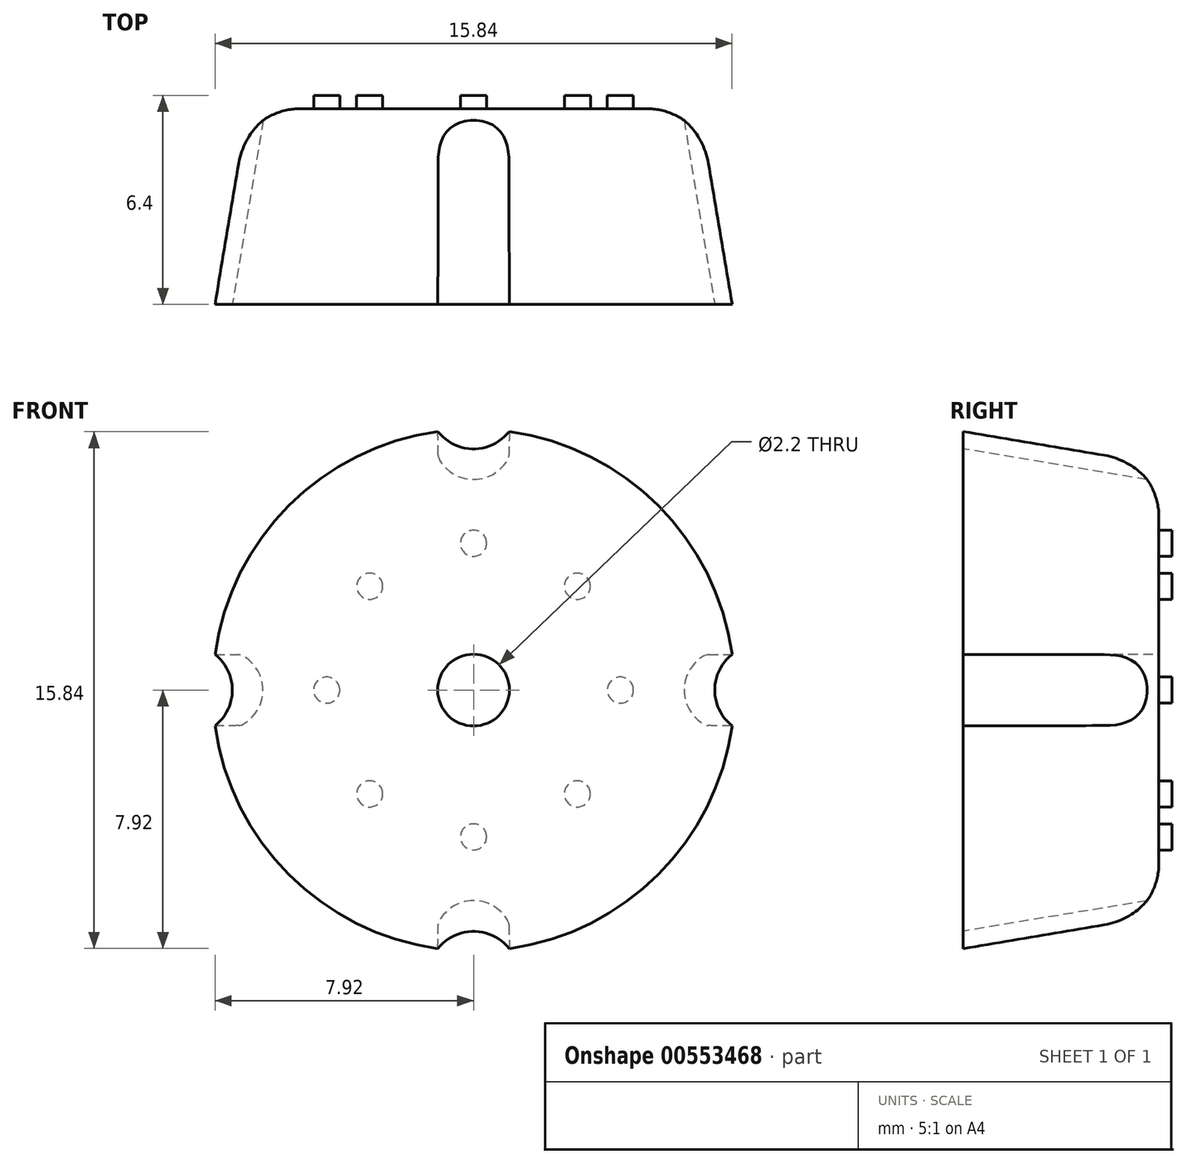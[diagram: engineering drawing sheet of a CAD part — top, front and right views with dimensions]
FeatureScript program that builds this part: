
annotation { "Feature Type Name" : "Feature", "Feature Type Description" : "" }
export const myFeature = defineFeature(function(context is Context, id is Id, definition is map)
    precondition{}
    {
        {
            var Q0;
            Q0=qCreatedBy(makeId("Top.planeOp"),FACE);
            var sketch = newSketch(context, id + "F0", { "sketchPlane" : qUnion([Q0])});
            skLineSegment(sketch, "E0", {"start": v(0, 0) * mm, "end": v(0, 26.8) * mm, "construction": true});
            skLineSegment(sketch, "E1", {"start": v(0, 0) * mm, "end": v(-8, 0) * mm});
            skLineSegment(sketch, "E2", {"start": v(-8, 0) * mm, "end": v(-7.28, 4.33) * mm});
            skLineSegment(sketch, "E3", {"start": v(-5.3, 6) * mm, "end": v(0, 6) * mm});
            skLineSegment(sketch, "E4", {"start": v(0, 6) * mm, "end": v(0, 0) * mm});
            skPoint(sketch, "E5.visualSharp", {"position": v(-7, 6) * mm});
            skArc(sketch, "E5.filletArc", {"start": v(-5.3, 6) * mm, "mid": v(-6.6, 5.53) * mm, "end": v(-7.28, 4.33) * mm});
            skSolve(sketch);
        }
        {
            var Q0;
            Q0 = qSketchRegion(id + "F0", true);
            var Q1;
            Q1=sQuery(id+"F0.wireOp",EDGE,"E0");
            revolve(context, id + "F1", {"entities" : qUnion([Q0]), "axis" : qUnion([Q1]), "revolveType" : RevolveType.FULL});
        }
        {
            var Q0;
            Q0=makeQuery(id+"F1.opRevolve","SWEPT_FACE",FACE,{"disambiguationData":[OSD([sQuery(id+"F0.wireOp",EDGE,"E3")])]});
            var sketch = newSketch(context, id + "F2", { "sketchPlane" : qUnion([Q0])});
            skCircle(sketch, "E6", {"center": v(0, 0) * mm, "radius": 4.5 * mm, "construction": true});
            skCircle(sketch, "E7", {"center": v(0, 4.5) * mm, "radius": 0.4 * mm});
            skCircle(sketch, "E8", {"center": v(4.5, 0) * mm, "radius": 0.4 * mm});
            skCircle(sketch, "E9", {"center": v(0, -4.5) * mm, "radius": 0.4 * mm});
            skCircle(sketch, "E10", {"center": v(-4.5, 0) * mm, "radius": 0.4 * mm});
            skLineSegment(sketch, "E11", {"start": v(-6.52, 6.52) * mm, "end": v(7.02, -7.02) * mm, "construction": true});
            skLineSegment(sketch, "E12", {"start": v(-6.76, -6.76) * mm, "end": v(6.87, 6.87) * mm, "construction": true});
            skCircle(sketch, "E13", {"center": v(-3.18, 3.18) * mm, "radius": 0.4 * mm});
            skCircle(sketch, "E14", {"center": v(3.18, 3.18) * mm, "radius": 0.4 * mm});
            skCircle(sketch, "E15", {"center": v(3.18, -3.18) * mm, "radius": 0.4 * mm});
            skCircle(sketch, "E16", {"center": v(-3.18, -3.18) * mm, "radius": 0.4 * mm});
            skSolve(sketch);
        }
        {
            var Q0;
            Q0 = qSketchRegion(id + "F2", true);
            extrude(context, id + "F3", {"entities" : qUnion([Q0]), "operationType" : NewBodyOperationType.ADD, "depth" : 0.4 * mm, "offsetDistance" : 25 * mm});
        }
        {
            var Q0;
            Q0=qCreatedBy(makeId("Right.planeOp"),FACE);
            var sketch = newSketch(context, id + "F4", { "sketchPlane" : qUnion([Q0])});
            skLineSegment(sketch, "E17", {"start": v(-1.6, 9.08) * mm, "end": v(12.64, 6.7) * mm, "construction": true});
            skLineSegment(sketch, "E18", {"start": v(0, 8) * mm, "end": v(4.33, 7.28) * mm, "construction": true});
            skLineSegment(sketch, "E19", {"start": v(4.33, -7.28) * mm, "end": v(0, -8) * mm, "construction": true});
            skLineSegment(sketch, "E20.0", {"start": v(4.33, -7.28) * mm, "end": v(4.33, 7.28) * mm, "construction": true});
            skLineSegment(sketch, "E21", {"start": v(-0.67, 8.92) * mm, "end": v(-0.44, 10.3) * mm});
            skLineSegment(sketch, "E22", {"start": v(-0.44, 10.3) * mm, "end": v(6.8, 9.1) * mm});
            skLineSegment(sketch, "E23", {"start": v(6.8, 9.1) * mm, "end": v(6.58, 7.71) * mm});
            skLineSegment(sketch, "E24", {"start": v(6.58, 7.71) * mm, "end": v(-0.67, 8.92) * mm});
            skSolve(sketch);
        }
        {
            var Q0;
            Q0 = qSketchRegion(id + "F4", true);
            var Q1;
            Q1=sQuery(id+"F4.wireOp",EDGE,"E17");
            revolve(context, id + "F5", {"entities" : qUnion([Q0]), "axis" : qUnion([Q1]), "revolveType" : RevolveType.FULL});
        }
        {
            var Q0;
            Q0=makeQuery(id+"F5.opRevolve","SWEPT_BODY",BODY,{"disambiguationData":[OSD([sQuery(id+"F4.wireOp",EDGE,"E21"),sQuery(id+"F4.wireOp",EDGE,"E22"),sQuery(id+"F4.wireOp",EDGE,"E23"),sQuery(id+"F4.wireOp",EDGE,"E24")])]});
            var Q1;
            Q1=makeQuery(id+"F1.opRevolve","SWEPT_EDGE",EDGE,{"disambiguationData":[OSD([sQuery(id+"F0.wireOp",EDGE,"E1"),sQuery(id+"F0.wireOp",EDGE,"E2")])]});
            circularPattern(context, id + "F6", {"entities" : qUnion([Q0]), "axis" : qUnion([Q1]), "angle" : 360 * degree, "instanceCount" : 4, "equalSpace" : true});
        }
        {
            var Q0;
            Q0=makeQuery(id+"F5.opRevolve","SWEPT_BODY",BODY,{"disambiguationData":[OSD([sQuery(id+"F4.wireOp",EDGE,"E21"),sQuery(id+"F4.wireOp",EDGE,"E22"),sQuery(id+"F4.wireOp",EDGE,"E23"),sQuery(id+"F4.wireOp",EDGE,"E24")])]});
            var Q1;
            Q1=makeQuery(id+"F6.opPattern","COPY",BODY,{"derivedFrom":makeQuery(id+"F5.opRevolve","SWEPT_BODY",BODY,{"disambiguationData":[OSD([sQuery(id+"F4.wireOp",EDGE,"E21"),sQuery(id+"F4.wireOp",EDGE,"E22"),sQuery(id+"F4.wireOp",EDGE,"E23"),sQuery(id+"F4.wireOp",EDGE,"E24")])]}),"instanceName":"1"});
            var Q2;
            Q2=makeQuery(id+"F6.opPattern","COPY",BODY,{"derivedFrom":makeQuery(id+"F5.opRevolve","SWEPT_BODY",BODY,{"disambiguationData":[OSD([sQuery(id+"F4.wireOp",EDGE,"E21"),sQuery(id+"F4.wireOp",EDGE,"E22"),sQuery(id+"F4.wireOp",EDGE,"E23"),sQuery(id+"F4.wireOp",EDGE,"E24")])]}),"instanceName":"2"});
            var Q3;
            Q3=makeQuery(id+"F6.opPattern","COPY",BODY,{"derivedFrom":makeQuery(id+"F5.opRevolve","SWEPT_BODY",BODY,{"disambiguationData":[OSD([sQuery(id+"F4.wireOp",EDGE,"E21"),sQuery(id+"F4.wireOp",EDGE,"E22"),sQuery(id+"F4.wireOp",EDGE,"E23"),sQuery(id+"F4.wireOp",EDGE,"E24")])]}),"instanceName":"3"});
            var Q4;
            Q4=makeQuery(id+"F1.opRevolve","SWEPT_BODY",BODY,{"disambiguationData":[OSD([sQuery(id+"F0.wireOp",EDGE,"E1"),sQuery(id+"F0.wireOp",EDGE,"E2"),sQuery(id+"F0.wireOp",EDGE,"E3"),sQuery(id+"F0.wireOp",EDGE,"E4"),sQuery(id+"F0.wireOp",EDGE,"E5.filletArc")])]});
            booleanBodies(context, id + "F7", {"operationType" : BooleanOperationType.SUBTRACTION, "tools" : qUnion([Q0, Q1, Q2, Q3]), "targets" : qUnion([Q4])});
        }
        {
            var Q0;
            Q0=makeQuery(id+"F1.opRevolve","SWEPT_FACE",FACE,{"disambiguationData":[OSD([sQuery(id+"F0.wireOp",EDGE,"E3")])]});
            var sketch = newSketch(context, id + "F8", { "sketchPlane" : qUnion([Q0])});
            skCircle(sketch, "E25", {"center": v(0, 0) * mm, "radius": 1.1 * mm});
            skSolve(sketch);
        }
        {
            var Q0;
            Q0 = qSketchRegion(id + "F8", true);
            extrude(context, id + "F9", {"entities" : qUnion([Q0]), "operationType" : NewBodyOperationType.REMOVE, "endBound" : BoundingType.THROUGH_ALL, "oppositeDirection" : true, "depth" : 25 * mm, "offsetDistance" : 25 * mm});
        }
    });
